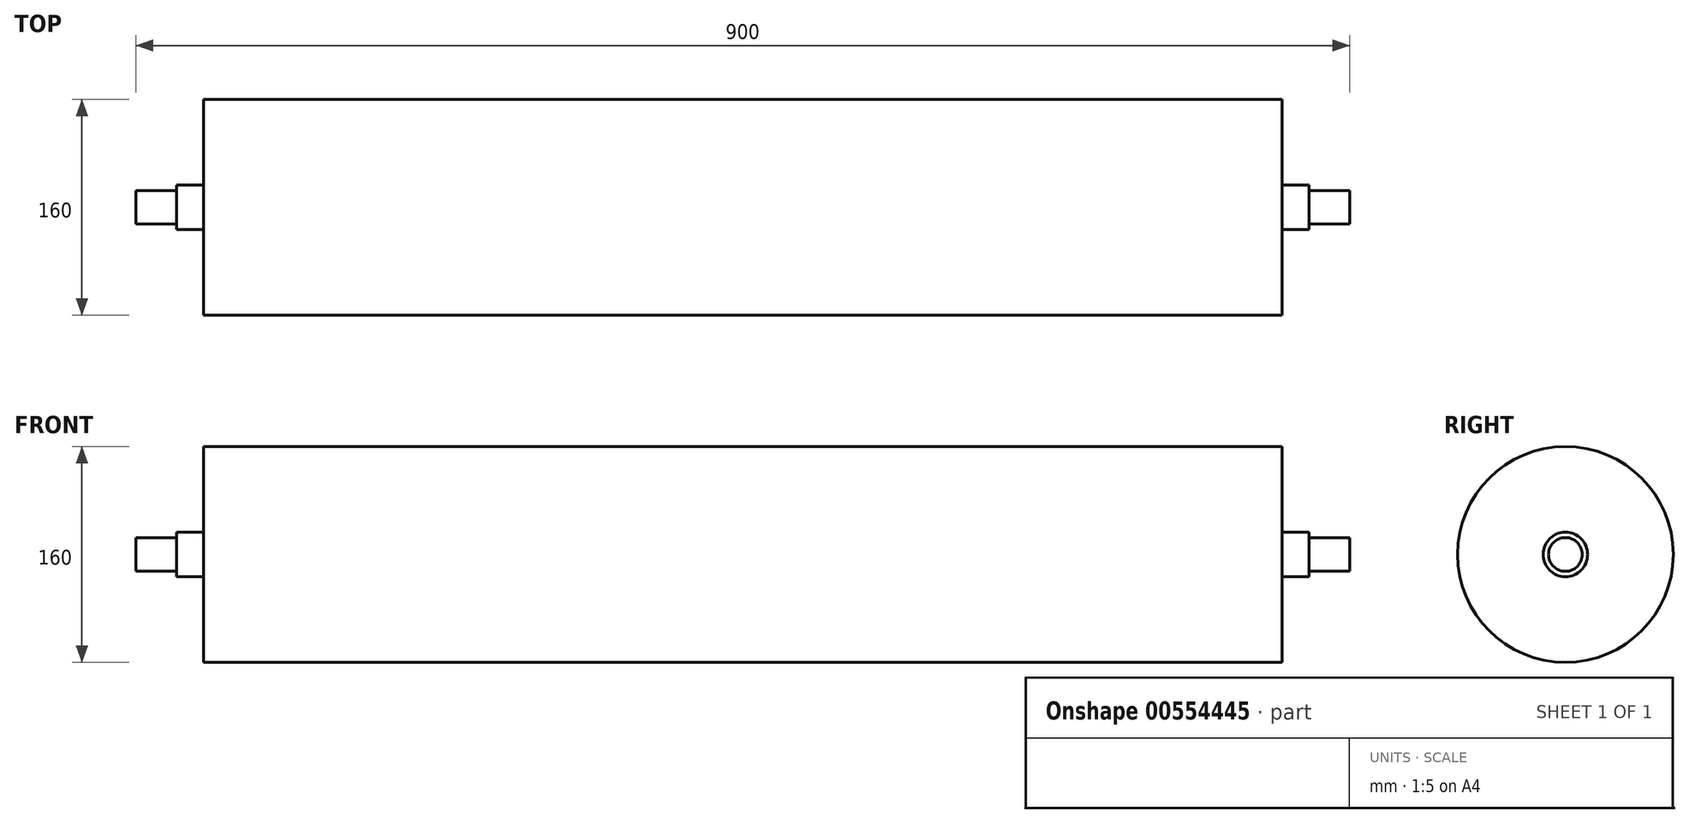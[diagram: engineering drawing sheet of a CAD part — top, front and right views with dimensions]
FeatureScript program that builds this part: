
annotation { "Feature Type Name" : "Feature", "Feature Type Description" : "" }
export const myFeature = defineFeature(function(context is Context, id is Id, definition is map)
    precondition{}
    {
        {
            var Q0;
            Q0=qCreatedBy(makeId("Front.planeOp"),FACE);
            var sketch = newSketch(context, id + "F0", { "sketchPlane" : qUnion([Q0])});
            skLineSegment(sketch, "E0", {"start": v(-450, 100) * mm, "end": v(0, 100) * mm});
            skLineSegment(sketch, "E1", {"start": v(0, 100) * mm, "end": v(450, 100) * mm});
            skLineSegment(sketch, "E2", {"start": v(450, 100) * mm, "end": v(450, 112.5) * mm});
            skLineSegment(sketch, "E3", {"start": v(450, 112.5) * mm, "end": v(420, 112.5) * mm});
            skLineSegment(sketch, "E4", {"start": v(420, 112.5) * mm, "end": v(420, 116.5) * mm});
            skLineSegment(sketch, "E5", {"start": v(420, 116.5) * mm, "end": v(400, 116.5) * mm});
            skLineSegment(sketch, "E6", {"start": v(400, 116.5) * mm, "end": v(400, 180) * mm});
            skLineSegment(sketch, "E7", {"start": v(400, 180) * mm, "end": v(-400, 180) * mm});
            skLineSegment(sketch, "E8", {"start": v(-400, 180) * mm, "end": v(-400, 116.5) * mm});
            skLineSegment(sketch, "E9", {"start": v(-400, 116.5) * mm, "end": v(-420, 116.5) * mm});
            skLineSegment(sketch, "E10", {"start": v(-420, 116.5) * mm, "end": v(-420, 112.5) * mm});
            skLineSegment(sketch, "E11", {"start": v(-420, 112.5) * mm, "end": v(-450, 112.5) * mm});
            skLineSegment(sketch, "E12", {"start": v(-450, 112.5) * mm, "end": v(-450, 100) * mm});
            skLineSegment(sketch, "E13", {"start": v(-466.17, 100) * mm, "end": v(477.17, 100) * mm, "construction": true});
            skSolve(sketch);
        }
        {
            var Q0;
            Q0=makeQuery(id+"F0.imprint","IMPRINT",FACE,{"disambiguationData":[TD([[makeQuery(id+"F0.imprint","IMPRINT",EDGE,{"derivedFrom":sQuery(id+"F0.wireOp",EDGE,"E0")}),1.0]])]});
            var Q1;
            Q1=sQuery(id+"F0.wireOp",EDGE,"E13");
            revolve(context, id + "F1", {"entities" : qUnion([Q0]), "axis" : qUnion([Q1]), "revolveType" : RevolveType.FULL});
        }
    });
